# Revit family: Floor_Mount_Double_Compartment_Scullery_Sink-Elkay-WNSF8248LR2
name_source: partatom
category: Plumbing Fixtures
units: mm (PartAtom-declared; Revit-internal decimal feet)

## family parameters
Always vertical = Yes
Cut with Voids When Loaded = No
Maintain Annotation Orientation = No
OmniClass Number = 23.45.05.14.14
OmniClass Title = Sinks/Lavatories
Part Type = Normal
Room Calculation Point = No
Round Connector Dimension = Use Diameter
Shared = No
Work Plane-Based = No

## types (1)
- WNSF8248LR2 (Floor Mount Double Compartment Scullery Sink with Drainboards)
    Approx. Shipping Weight (lbs) = 224
    Assembly Code = D2010.60
    Bowl & Rim match DIM = 12.250"
    Bowl 1 Dimensions = 24 inch x 24 inch x 14 inch
    Bowl 2 Dimensions = 24 inch x 24 inch x 14 inch
    Bowl Length = 48.000"
    Bowl Profile Dist = 11.750"
    Bowl Width = 24.000"
    Default Elevation = 0.000"
    Description = Weldbilt® Stainless Steel 96 inch x 27 1/2 inch x 14 inch Floor Mount Double Compartment Scullery Sink with Drainboard
    Drain Board Length = 24.000"
    Drain Location = Center
    Drain Size = 3.500"
    Drainbd radius1 = 0.150"
    Drainbd radius2 = 0.075"
    Drainboard Location = Left and Right
    Drainboard fini = 22.575"
    Drainboard ini = 24.000"
    Drainboard width = 24.000"
    Installation Type = Floor Mount
    Legs Dist. X = 43.250"
    Legs Dist. Y = 19.250"
    Main Material = Finish-Elkay-Stainless Steel
    Manufacturer = Elkay Manufacturer Company
    Manufacturer Brand = Elkay (by Zurn Elkay Water Solutions)
    Model = WNSF8248LR2
    No of Bowls = 2
    Outlet Connection Size (inch) = 1.500"
    Product Documentation Link = https://www.elkayfiles.com
    Product Page URL = https://www.elkay.com
    Product Weight (lbs) = 164
    Product data URL = https://www.bimobject.com
    Rim Width = 25.500"
    Sink Dimensions = 96 inch x 27 1/2 inch x 44 inch
    Sink Length = 96.000"
    Sink Width = 27.500"
    Sweep Profile Dist = 48.000"
    URL = https://www.elkay.com

## geometry (parser evidence)
native form markers: Sweep x2
no freeform markers — native parametric forms only
